# Revit family: Enclosures for IEC
name_source: partatom
category: Installations électriques
revit_build: Autodesk Revit 2018 (Build: 20170223_1515(x64)
units: mm (PartAtom-declared; Revit-internal decimal feet)

## family parameters
Conserver l'orientation des annotations = Non
Cote de connecteur circulaire = Utiliser le diamètre
Couper avec des vides une fois chargée = Non
Hôte = Face
Partagée = Oui
Point de calcul de pièce = Non
Type d'élément = Normal

## types (1)
- For one 16A or 32A panel mounting socket with inclined outlet
    Description = Enclosure for the assembly of connectors to the international standard
    Diameter cable entry = PG16/PG21
    Elévation par défaut = 1000 mm  [stored 3.28084 ft]
    Fabricant = Legrand
    IDS_MONTAGE_PRISE_VERROUILLEE = Non
    Maximum use temperature = 40°C
    Minimum use temperature = -25°C
    Modèle = LG-057750
    Product family = 0852-P17
    depth mm = 97 mm
    halogen free = Oui
    height mm = 97 mm
    horizontal fixing distance mm = 75 mm
    intensity A = 16 A
    material of box = plastic
    resistance to chocks IK = 08
    vertical fixing distance mm = 85 mm
    width mm = 87 mm

note: [stored X ft] marks values corroborated as IEEE doubles in the binary element streams (Revit-internal decimal feet)
